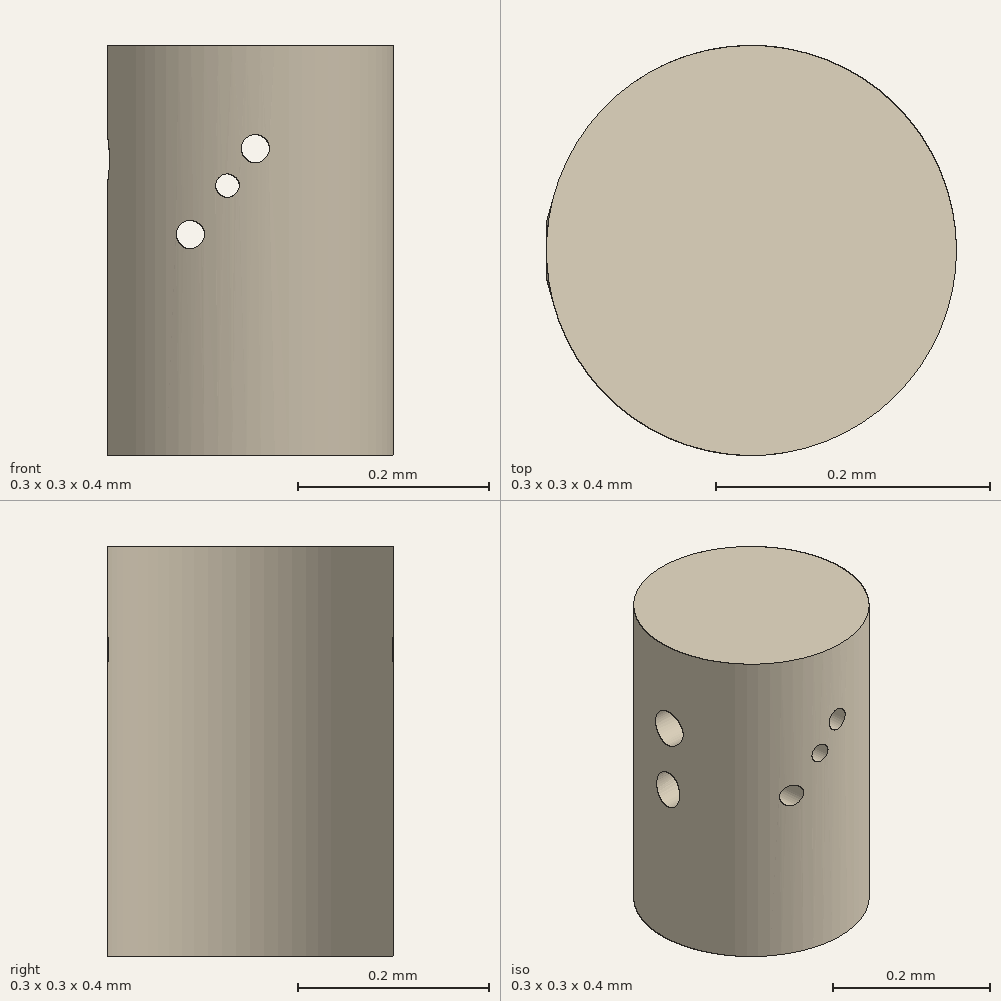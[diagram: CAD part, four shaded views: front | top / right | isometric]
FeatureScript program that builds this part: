
annotation { "Feature Type Name" : "Feature", "Feature Type Description" : "" }
export const myFeature = defineFeature(function(context is Context, id is Id, definition is map)
    precondition{}
    {
        {
            var Q0;
            Q0=qCreatedBy(makeId("Top.planeOp"),FACE);
            var sketch = newSketch(context, id + "F0", { "sketchPlane" : qUnion([Q0])});
            skCircle(sketch, "E0", {"center": v(0, 0) * mm, "radius": 0.15 * mm});
            skSolve(sketch);
        }
        {
            var Q0;
            Q0=qSketchRegion(id+"F0",true);
            extrude(context, id + "F1", {"entities" : qUnion([Q0]), "depth" : 0.43 * mm, "offsetDistance" : 25 * mm});
        }
        {
            var Q0;
            Q0=qCreatedBy(makeId("Top.planeOp"),FACE);
            var sketch = newSketch(context, id + "F2", { "sketchPlane" : qUnion([Q0])});
            skCircle(sketch, "E1", {"center": v(0, 0) * mm, "radius": 0.07 * mm});
            skSolve(sketch);
        }
        {
            var Q0;
            Q0=qSketchRegion(id+"F2",true);
            extrude(context, id + "F3", {"entities" : qUnion([Q0]), "operationType" : NewBodyOperationType.REMOVE, "depth" : 0.1 * mm, "offsetDistance" : 25 * mm});
        }
        {
            var Q0;
            Q0=qCreatedBy(makeId("Front.planeOp"),FACE);
            var sketch = newSketch(context, id + "F4", { "sketchPlane" : qUnion([Q0])});
            skLineSegment(sketch, "E2", {"start": v(0, 0.1) * mm, "end": v(0, 0.27) * mm});
            skLineSegment(sketch, "E3", {"start": v(0, 0.27) * mm, "end": v(1, -0.74) * mm, "construction": true});
            skLineSegment(sketch, "E4", {"start": v(1, -0.74) * mm, "end": v(0.06, 0.32) * mm, "construction": true});
            skLineSegment(sketch, "E5", {"start": v(1, -0.74) * mm, "end": v(-0.07, 0.19) * mm, "construction": true});
            skArc(sketch, "E6", {"start": v(-0.07, 0.19) * mm, "mid": v(0, 0.26) * mm, "end": v(0.06, 0.32) * mm});
            skLineSegment(sketch, "E7", {"start": v(-0.07, 0.19) * mm, "end": v(-0.1, 0.21) * mm});
            skLineSegment(sketch, "E8", {"start": v(-0.1, 0.21) * mm, "end": v(0, 0.36) * mm});
            skLineSegment(sketch, "E9", {"start": v(0, 0.36) * mm, "end": v(0.06, 0.32) * mm});
            skSolve(sketch);
        }
        {
            var Q0;
            Q0=qSketchRegion(id+"F4",true);
            extrude(context, id + "F5", {"entities" : qUnion([Q0]), "operationType" : NewBodyOperationType.REMOVE, "oppositeDirection" : true, "depth" : 0.05 * mm, "offsetDistance" : 25 * mm});
        }
        {
            var Q0;
            Q0=qSketchRegion(id+"F4",true);
            extrude(context, id + "F6", {"entities" : qUnion([Q0]), "operationType" : NewBodyOperationType.REMOVE, "depth" : 0.05 * mm, "offsetDistance" : 25 * mm});
        }
        {
            var Q0;
            Q0=qCreatedBy(makeId("Front.planeOp"),FACE);
            var sketch = newSketch(context, id + "F7", { "sketchPlane" : qUnion([Q0])});
            skCircle(sketch, "E10", {"center": v(-0.06, 0.23) * mm, "radius": 0.02 * mm});
            skCircle(sketch, "E11", {"center": v(0, 0.32) * mm, "radius": 0.02 * mm});
            skCircle(sketch, "E12", {"center": v(-0.02, 0.28) * mm, "radius": 0.01 * mm});
            skSolve(sketch);
        }
        {
            var Q0;
            Q0=qSketchRegion(id+"F7",true);
            extrude(context, id + "F8", {"entities" : qUnion([Q0]), "operationType" : NewBodyOperationType.REMOVE, "oppositeDirection" : true, "depth" : 1 * mm, "offsetDistance" : 25 * mm});
        }
        {
            var Q0;
            Q0=qSketchRegion(id+"F7",true);
            extrude(context, id + "F9", {"entities" : qUnion([Q0]), "operationType" : NewBodyOperationType.REMOVE, "depth" : 1 * mm, "offsetDistance" : 25 * mm});
        }
        {
            var Q0;
            Q0=qCreatedBy(makeId("Right.planeOp"),FACE);
            var sketch = newSketch(context, id + "F10", { "sketchPlane" : qUnion([Q0])});
            skCircle(sketch, "E13", {"center": v(0, 0.31) * mm, "radius": 0.03 * mm});
            skSolve(sketch);
        }
        {
            var Q0;
            Q0=qSketchRegion(id+"F10",true);
            extrude(context, id + "F11", {"entities" : qUnion([Q0]), "operationType" : NewBodyOperationType.REMOVE, "oppositeDirection" : true, "depth" : 1 * mm, "offsetDistance" : 25 * mm});
        }
        {
            var Q0;
            Q0=qSketchRegion(id+"F10",true);
            extrude(context, id + "F12", {"entities" : qUnion([Q0]), "operationType" : NewBodyOperationType.REMOVE, "depth" : 0.01 * mm, "offsetDistance" : 25 * mm});
        }
        {
            var Q0;
            Q0=qCreatedBy(makeId("Right.planeOp"),FACE);
            cPlane(context, id + "F13", {"entities" : qUnion([Q0]), "cplaneType" : CPlaneType.OFFSET, "offset" : 0.15 * mm, "oppositeDirection" : true, "width" : 150 * mm, "height" : 150 * mm});
        }
        {
            var Q0;
            Q0=qCreatedBy(id+"F13.planeOp",FACE);
            var sketch = newSketch(context, id + "F14", { "sketchPlane" : qUnion([Q0])});
            skCircle(sketch, "E14", {"center": v(0, 0.22) * mm, "radius": 0.03 * mm});
            skSolve(sketch);
        }
        {
            var Q0;
            Q0=qSketchRegion(id+"F14",true);
            extrude(context, id + "F15", {"entities" : qUnion([Q0]), "operationType" : NewBodyOperationType.REMOVE, "depth" : 0.08 * mm, "offsetDistance" : 25 * mm});
        }
    });
